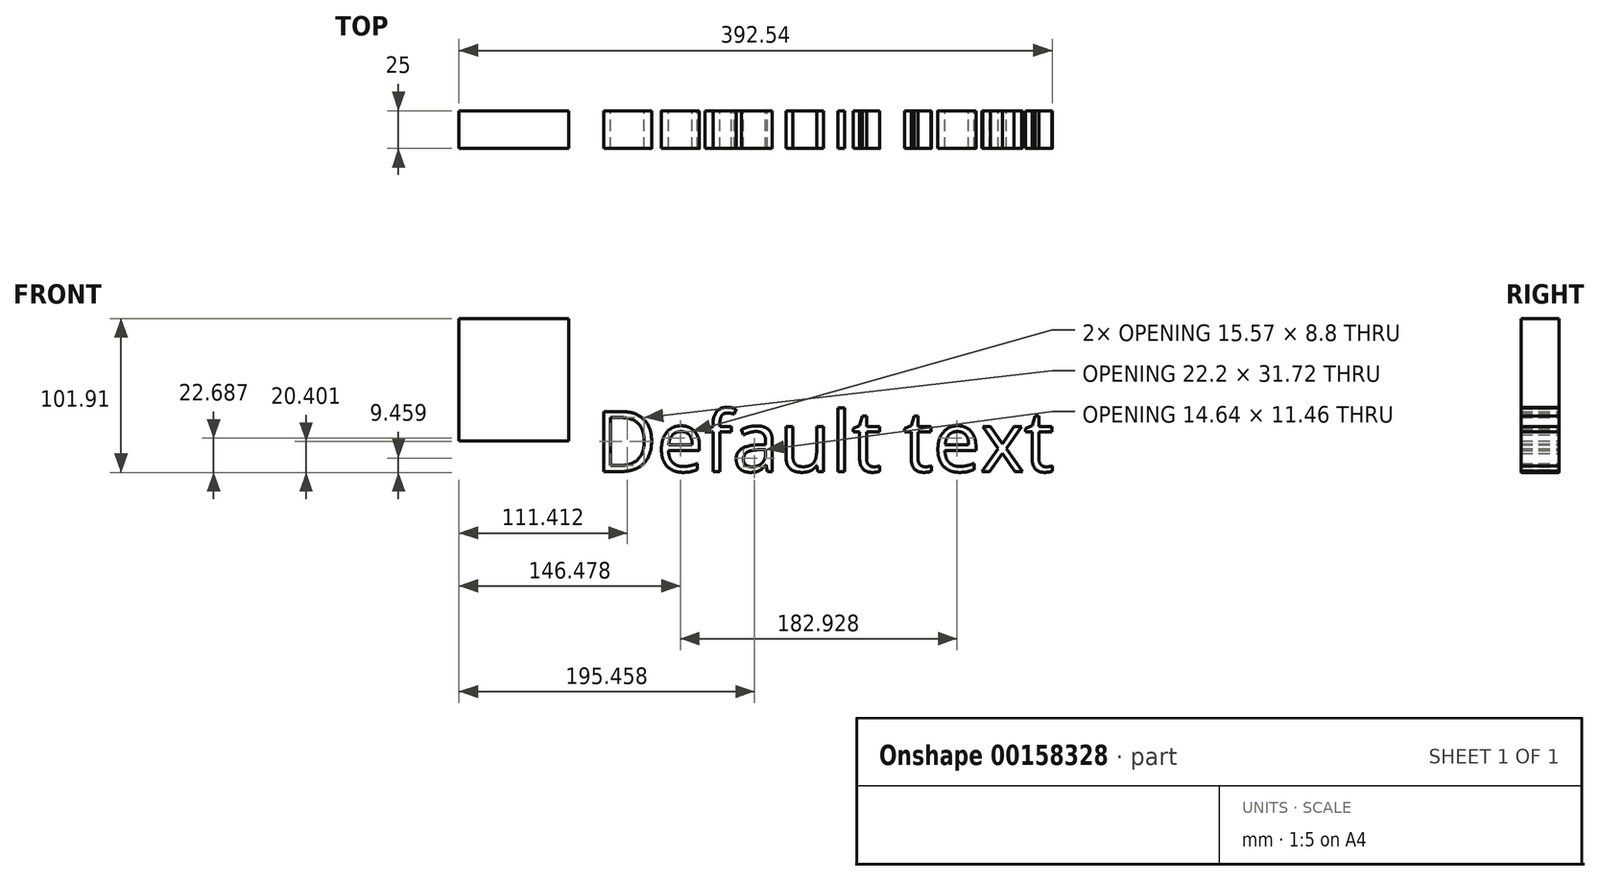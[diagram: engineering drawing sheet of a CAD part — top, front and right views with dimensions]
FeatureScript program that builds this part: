
annotation { "Feature Type Name" : "Feature", "Feature Type Description" : "" }
export const myFeature = defineFeature(function(context is Context, id is Id, definition is map)
    precondition{}
    {
        {
            var Q0;
            Q0=qCreatedBy(makeId("Front.planeOp"),FACE);
            var sketch = newSketch(context, id + "F0", { "sketchPlane" : qUnion([Q0])});
            skLineSegment(sketch, "E0.bottom", {"start": v(-47.58, 81.22) * mm, "end": v(25.02, 81.22) * mm});
            skLineSegment(sketch, "E0.top", {"start": v(-47.58, 0) * mm, "end": v(25.02, 0) * mm});
            skLineSegment(sketch, "E0.left", {"start": v(-47.58, 81.22) * mm, "end": v(-47.58, 0) * mm});
            skLineSegment(sketch, "E0.right", {"start": v(25.02, 81.22) * mm, "end": v(25.02, 0) * mm});
            skSolve(sketch);
        }
        {
            var Q0;
            Q0=makeQuery(id+"F0.imprint","IMPRINT",FACE,{"disambiguationData":[TD([[makeQuery(id+"F0.imprint","IMPRINT",EDGE,{"derivedFrom":sQuery(id+"F0.wireOp",EDGE,"E0.bottom")}),-1.0]])]});
            extrude(context, id + "F1", {"entities" : qUnion([Q0]), "depth" : 25 * mm});
        }
        {
            var Q0;
            Q0=qCreatedBy(makeId("Front.planeOp"),FACE);
            var sketch = newSketch(context, id + "F2", { "sketchPlane" : qUnion([Q0])});
            skText(sketch, "E1", { "text": "Default text", "fontName": "OpenSans-Regular.ttf"});
            const initialGuessF2  = {"E1": [0.04266, -0.02014, 1, 0, 0.04005]};
            skSetInitialGuess(sketch, initialGuessF2);
            skSolve(sketch);
        }
        {
            var Q0;
            Q0 = qSketchRegion(id + "F2", true);
            extrude(context, id + "F3", {"entities" : qUnion([Q0]), "depth" : 25 * mm});
        }
    });
